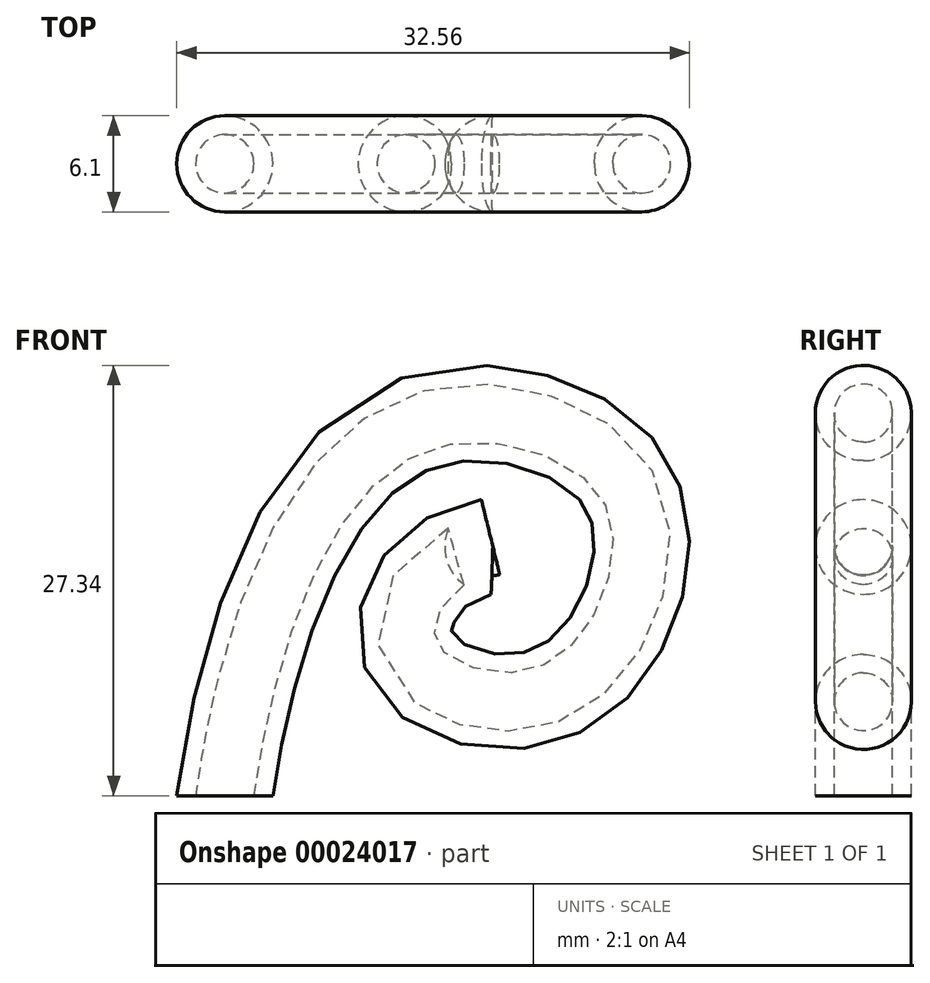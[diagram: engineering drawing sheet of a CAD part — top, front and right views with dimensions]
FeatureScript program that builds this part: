
annotation { "Feature Type Name" : "Feature", "Feature Type Description" : "" }
export const myFeature = defineFeature(function(context is Context, id is Id, definition is map)
    precondition{}
    {
        {
            var Q0;
            Q0=qCreatedBy(makeId("Top.planeOp"),FACE);
            var sketch = newSketch(context, id + "F0", { "sketchPlane" : qUnion([Q0])});
            skCircle(sketch, "E0", {"center": v(0, 0) * mm, "radius": 1.85 * mm});
            skCircle(sketch, "E1", {"center": v(0, 0) * mm, "radius": 3.05 * mm});
            skSolve(sketch);
        }
        {
            var Q0;
            Q0=qCreatedBy(makeId("Front.planeOp"),FACE);
            var sketch = newSketch(context, id + "F1", { "sketchPlane" : qUnion([Q0])});
            skFitSpline(sketch, "E2", {"points": [v(0, 0) * mm, v(4.2, 15.2) * mm, v(13.58, 24.06) * mm, v(25.08, 20.46) * mm, v(25.5, 11.57) * mm, v(19.23, 6.09) * mm, v(11.75, 9.13) * mm, v(17.02, 15.84) * mm], "startDerivative": vector(9.83, 72.44) * mm, "endDerivative": vector(101.17, 10.68) * mm});
            skSolve(sketch);
        }
        {
            var Q0;
            Q0=makeQuery(id+"F0.imprint","IMPRINT",FACE,{"disambiguationData":[TD([[makeQuery(id+"F0.imprint","IMPRINT",EDGE,{"derivedFrom":sQuery(id+"F0.wireOp",EDGE,"E0")}),-1.0]])]});
            var Q1;
            Q1=sQuery(id+"F1.wireOp",EDGE,"E2");
            sweep(context, id + "F2", {"profiles" : qUnion([Q0]), "path" : qUnion([Q1])});
        }
        {
            var Q0;
            Q0=makeQuery(id+"F2.opSweep","CAP_FACE",FACE,{"disambiguationData":[OSD([sQuery(id+"F0.wireOp",EDGE,"E0"),sQuery(id+"F0.wireOp",EDGE,"E1"),sQuery(id+"F1.wireOp",VERTEX,"E2.end")])],"isStart":false});
            var sketch = newSketch(context, id + "F3", { "sketchPlane" : qUnion([Q0])});
            skLineSegment(sketch, "E3", {"start": v(0, 14.4) * mm, "end": v(0, 8.3) * mm});
            skSolve(sketch);
        }
        {
            var Q0;
            {var subQ0=sQuery(id+"F3.wireOp",EDGE,"E3");var subQ1=sQuery(id+"F1.wireOp",VERTEX,"E2.end");var subQ2=makeQuery(id+"F2.opSweep","CAP_EDGE",EDGE,{"disambiguationData":[OSD([sQuery(id+"F0.wireOp",EDGE,"E1"),subQ1])],"isStart":false});var subQ3=makeQuery(id+"F3.imprint","INTERSECT",VERTEX,{"disambiguationData":[OD(0.0)],"derivedFrom":[subQ2,subQ0]});Q0=makeQuery(id+"F3.imprint","IMPRINT",FACE,{"disambiguationData":[TD([[makeQuery(id+"F3.imprint","IMPRINT",EDGE,{"disambiguationData":[TD([[subQ3,-1.0]])],"derivedFrom":subQ0}),-1.0]])]});}
            var Q1;
            Q1=sQuery(id+"F3.wireOp",EDGE,"E3");
            revolve(context, id + "F4", {"operationType" : NewBodyOperationType.ADD, "entities" : qUnion([Q0]), "axis" : qUnion([Q1]), "revolveType" : RevolveType.FULL});
        }
    });
